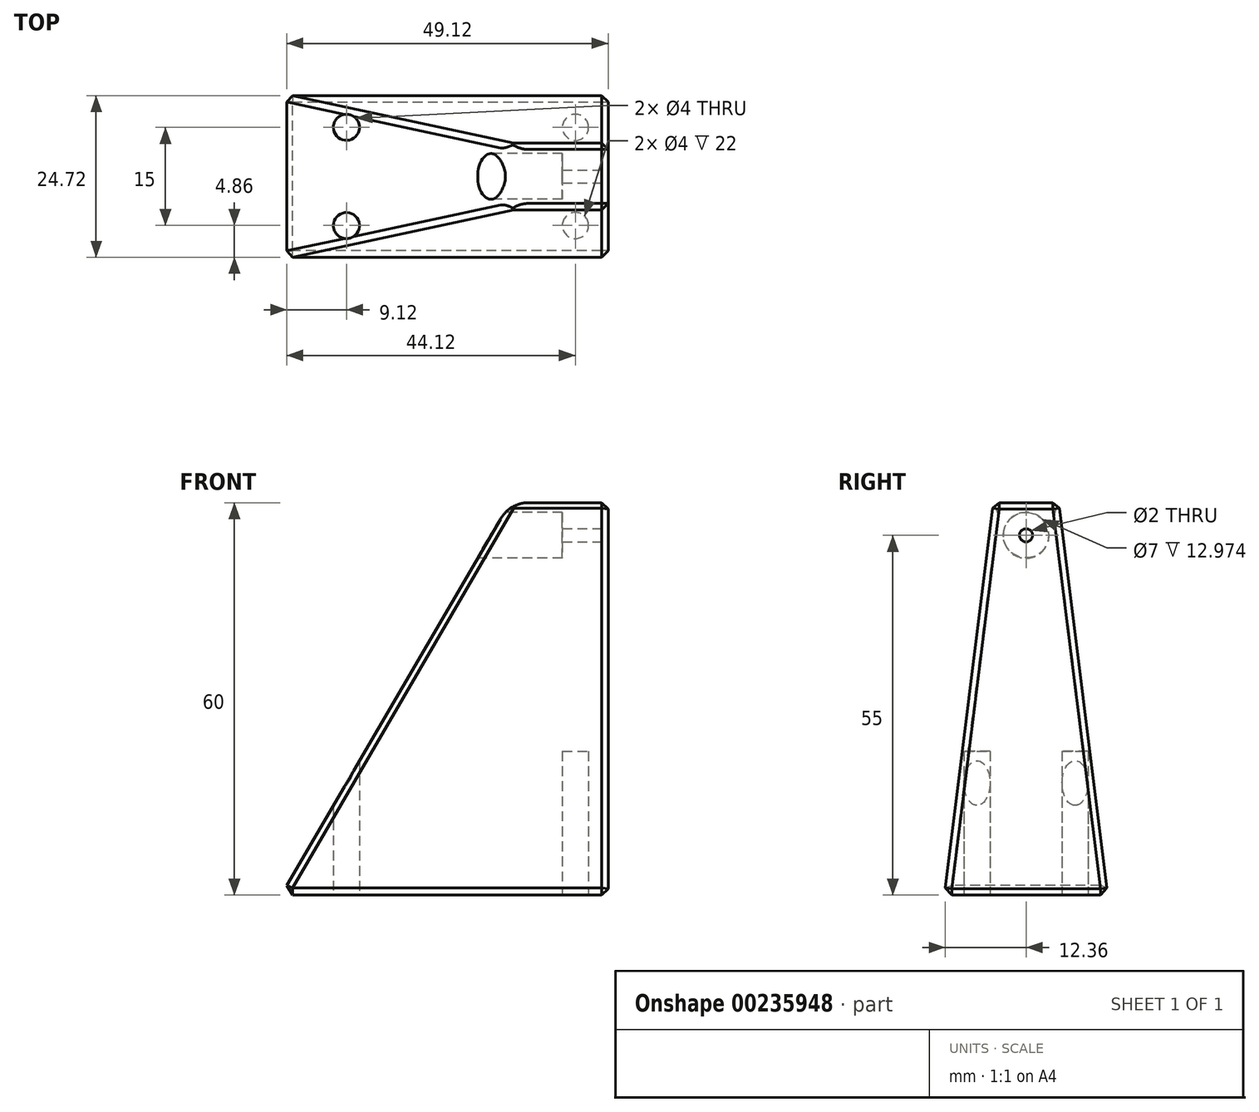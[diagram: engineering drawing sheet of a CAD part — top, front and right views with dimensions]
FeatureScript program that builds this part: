
annotation { "Feature Type Name" : "Feature", "Feature Type Description" : "" }
export const myFeature = defineFeature(function(context is Context, id is Id, definition is map)
    precondition{}
    {
        {
            var Q0;
            Q0=qCreatedBy(makeId("Top.planeOp"),FACE);
            var sketch = newSketch(context, id + "F0", { "sketchPlane" : qUnion([Q0])});
            skLineSegment(sketch, "E0.bottom", {"start": v(0, 0) * mm, "end": v(-50, 0) * mm});
            skLineSegment(sketch, "E0.top", {"start": v(0, -25) * mm, "end": v(-50, -25) * mm});
            skLineSegment(sketch, "E0.left", {"start": v(0, 0) * mm, "end": v(0, -25) * mm});
            skLineSegment(sketch, "E0.right", {"start": v(-50, 0) * mm, "end": v(-50, -25) * mm});
            skSolve(sketch);
        }
        {
            var Q0;
            Q0=qCreatedBy(makeId("Top.planeOp"),FACE);
            cPlane(context, id + "F1", {"entities" : qUnion([Q0]), "cplaneType" : CPlaneType.OFFSET, "offset" : 60 * mm, "width" : 150 * mm, "height" : 150 * mm});
        }
        {
            var Q0;
            Q0=qCreatedBy(id+"F1.planeOp",FACE);
            var sketch = newSketch(context, id + "F2", { "sketchPlane" : qUnion([Q0])});
            skLineSegment(sketch, "E1.bottom", {"start": v(0, -7.5) * mm, "end": v(-15, -7.5) * mm});
            skLineSegment(sketch, "E1.top", {"start": v(0, -17.5) * mm, "end": v(-15, -17.5) * mm});
            skLineSegment(sketch, "E1.left", {"start": v(0, -7.5) * mm, "end": v(0, -17.5) * mm});
            skLineSegment(sketch, "E1.right", {"start": v(-15, -7.5) * mm, "end": v(-15, -17.5) * mm});
            skSolve(sketch);
        }
        {
            var Q0;
            Q0=makeQuery(id+"F0.imprint","IMPRINT",FACE,{"disambiguationData":[TD([[makeQuery(id+"F0.imprint","IMPRINT",EDGE,{"derivedFrom":sQuery(id+"F0.wireOp",EDGE,"E0.bottom")}),1.0]])]});
            var Q1;
            Q1=makeQuery(id+"F2.imprint","IMPRINT",FACE,{"disambiguationData":[TD([[makeQuery(id+"F2.imprint","IMPRINT",EDGE,{"derivedFrom":sQuery(id+"F2.wireOp",EDGE,"E1.bottom")}),1.0]])]});
            loft(context, id + "F3", {"sheetProfilesArray" : [{ "sheetProfileEntities" : qUnion([Q0]) }, { "sheetProfileEntities" : qUnion([Q1]) }]});
        }
        {
            var Q0;
            Q0=makeQuery(id+"F3.opLoft","SWEPT_FACE",FACE,{"disambiguationData":[OSD([sQuery(id+"F0.wireOp",EDGE,"E0.bottom"),sQuery(id+"F0.wireOp",EDGE,"E0.top"),sQuery(id+"F0.wireOp",EDGE,"E0.left"),sQuery(id+"F2.wireOp",EDGE,"E1.bottom"),sQuery(id+"F2.wireOp",EDGE,"E1.top"),sQuery(id+"F2.wireOp",EDGE,"E1.left")])]});
            var sketch = newSketch(context, id + "F4", { "sketchPlane" : qUnion([Q0])});
            skCircle(sketch, "E2", {"center": v(-12.5, 55) * mm, "radius": 1 * mm});
            skLineSegment(sketch, "E3", {"start": v(-12.5, 55) * mm, "end": v(-17.5, 60) * mm, "construction": true});
            skLineSegment(sketch, "E4", {"start": v(-7.5, 60) * mm, "end": v(-12.5, 55) * mm, "construction": true});
            skSolve(sketch);
        }
        {
            var Q0;
            Q0 = qSketchRegion(id + "F4", true);
            extrude(context, id + "F5", {"entities" : qUnion([Q0]), "operationType" : NewBodyOperationType.REMOVE, "oppositeDirection" : true, "depth" : 25 * mm});
        }
        {
            var Q0;
            Q0=qCreatedBy(makeId("Right.planeOp"),FACE);
            cPlane(context, id + "F6", {"entities" : qUnion([Q0]), "cplaneType" : CPlaneType.OFFSET, "offset" : 25 * mm, "oppositeDirection" : true, "width" : 150 * mm, "height" : 150 * mm});
        }
        {
            var Q0;
            Q0=qCreatedBy(id+"F6.planeOp",FACE);
            var sketch = newSketch(context, id + "F7", { "sketchPlane" : qUnion([Q0])});
            skPoint(sketch, "E5.0", {"position": v(-12.5, 55) * mm});
            skCircle(sketch, "E6", {"center": v(-12.5, 55) * mm, "radius": 3.5 * mm});
            skCircle(sketch, "E7.0", {"center": v(-12.5, 55) * mm, "radius": 1 * mm, "construction": true});
            skSolve(sketch);
        }
        {
            var Q0;
            Q0 = qSketchRegion(id + "F7", true);
            extrude(context, id + "F8", {"entities" : qUnion([Q0]), "operationType" : NewBodyOperationType.REMOVE, "depth" : 18 * mm});
        }
        {
            var Q0;
            Q0=makeQuery(id+"F3.opLoft","CAP_FACE",FACE,{"disambiguationData":[OSD([makeQuery(id+"F0.imprint","IMPRINT",FACE,{"disambiguationData":[TD([[makeQuery(id+"F0.imprint","IMPRINT",EDGE,{"derivedFrom":sQuery(id+"F0.wireOp",EDGE,"E0.bottom")}),1.0]])]})])],"isStart":true});
            var sketch = newSketch(context, id + "F9", { "sketchPlane" : qUnion([Q0])});
            skLineSegment(sketch, "E8.bottom", {"start": v(-40, 5) * mm, "end": v(-5, 5) * mm, "construction": true});
            skLineSegment(sketch, "E8.top", {"start": v(-40, 20) * mm, "end": v(-5, 20) * mm, "construction": true});
            skLineSegment(sketch, "E8.left", {"start": v(-40, 5) * mm, "end": v(-40, 20) * mm, "construction": true});
            skLineSegment(sketch, "E8.right", {"start": v(-5, 5) * mm, "end": v(-5, 20) * mm, "construction": true});
            skCircle(sketch, "E9", {"center": v(-40, 5) * mm, "radius": 2 * mm});
            skCircle(sketch, "E10", {"center": v(-40, 20) * mm, "radius": 2 * mm});
            skCircle(sketch, "E11", {"center": v(-5, 20) * mm, "radius": 2 * mm});
            skCircle(sketch, "E12", {"center": v(-5, 5) * mm, "radius": 2 * mm});
            skSolve(sketch);
        }
        {
            var Q0;
            Q0 = qSketchRegion(id + "F9", true);
            extrude(context, id + "F10", {"entities" : qUnion([Q0]), "operationType" : NewBodyOperationType.REMOVE, "oppositeDirection" : true, "depth" : 22 * mm});
        }
        {
            var Q0;
            Q0=makeQuery(id+"F3.opLoft","SWEPT_FACE",FACE,{"disambiguationData":[OSD([sQuery(id+"F0.wireOp",EDGE,"E0.bottom"),sQuery(id+"F0.wireOp",EDGE,"E0.left"),sQuery(id+"F0.wireOp",EDGE,"E0.right"),sQuery(id+"F2.wireOp",EDGE,"E1.bottom"),sQuery(id+"F2.wireOp",EDGE,"E1.left"),sQuery(id+"F2.wireOp",EDGE,"E1.right")])]});
            var Q1;
            Q1=makeQuery(id+"F3.opLoft","SWEPT_FACE",FACE,{"disambiguationData":[OSD([sQuery(id+"F0.wireOp",EDGE,"E0.top"),sQuery(id+"F0.wireOp",EDGE,"E0.left"),sQuery(id+"F0.wireOp",EDGE,"E0.right"),sQuery(id+"F2.wireOp",EDGE,"E1.top"),sQuery(id+"F2.wireOp",EDGE,"E1.left"),sQuery(id+"F2.wireOp",EDGE,"E1.right")])]});
            var Q2;
            Q2=makeQuery(id+"F3.opLoft","MID_CAP_EDGE",EDGE,{"disambiguationData":[OSD([sQuery(id+"F2.wireOp",EDGE,"E1.bottom"),sQuery(id+"F2.wireOp",EDGE,"E1.top"),sQuery(id+"F2.wireOp",EDGE,"E1.left")])],"capPos":1.0});
            var Q3;
            Q3=makeQuery(id+"F3.opLoft","MID_CAP_EDGE",EDGE,{"disambiguationData":[OSD([sQuery(id+"F0.wireOp",EDGE,"E0.bottom"),sQuery(id+"F0.wireOp",EDGE,"E0.top"),sQuery(id+"F0.wireOp",EDGE,"E0.left")])],"capPos":0.0});
            var Q4;
            Q4=makeQuery(id+"F3.opLoft","MID_CAP_EDGE",EDGE,{"disambiguationData":[OSD([sQuery(id+"F0.wireOp",EDGE,"E0.bottom"),sQuery(id+"F0.wireOp",EDGE,"E0.top"),sQuery(id+"F0.wireOp",EDGE,"E0.right")])],"capPos":0.0});
            chamfer(context, id + "F11", {"entities" : qUnion([Q0, Q1, Q2, Q3, Q4]), "width" : 1 * mm, "tangentPropagation" : true});
        }
        {
            var Q0;
            Q0=makeQuery(id+"F3.opLoft","MID_CAP_EDGE",EDGE,{"disambiguationData":[OSD([sQuery(id+"F2.wireOp",EDGE,"E1.bottom"),sQuery(id+"F2.wireOp",EDGE,"E1.top"),sQuery(id+"F2.wireOp",EDGE,"E1.right")])],"capPos":1.0});
            fillet(context, id + "F12", {"entities" : qUnion([Q0]), "radius" : 5 * mm, "tangentPropagation" : true, "allowEdgeOverflow" : false});
        }
    });
